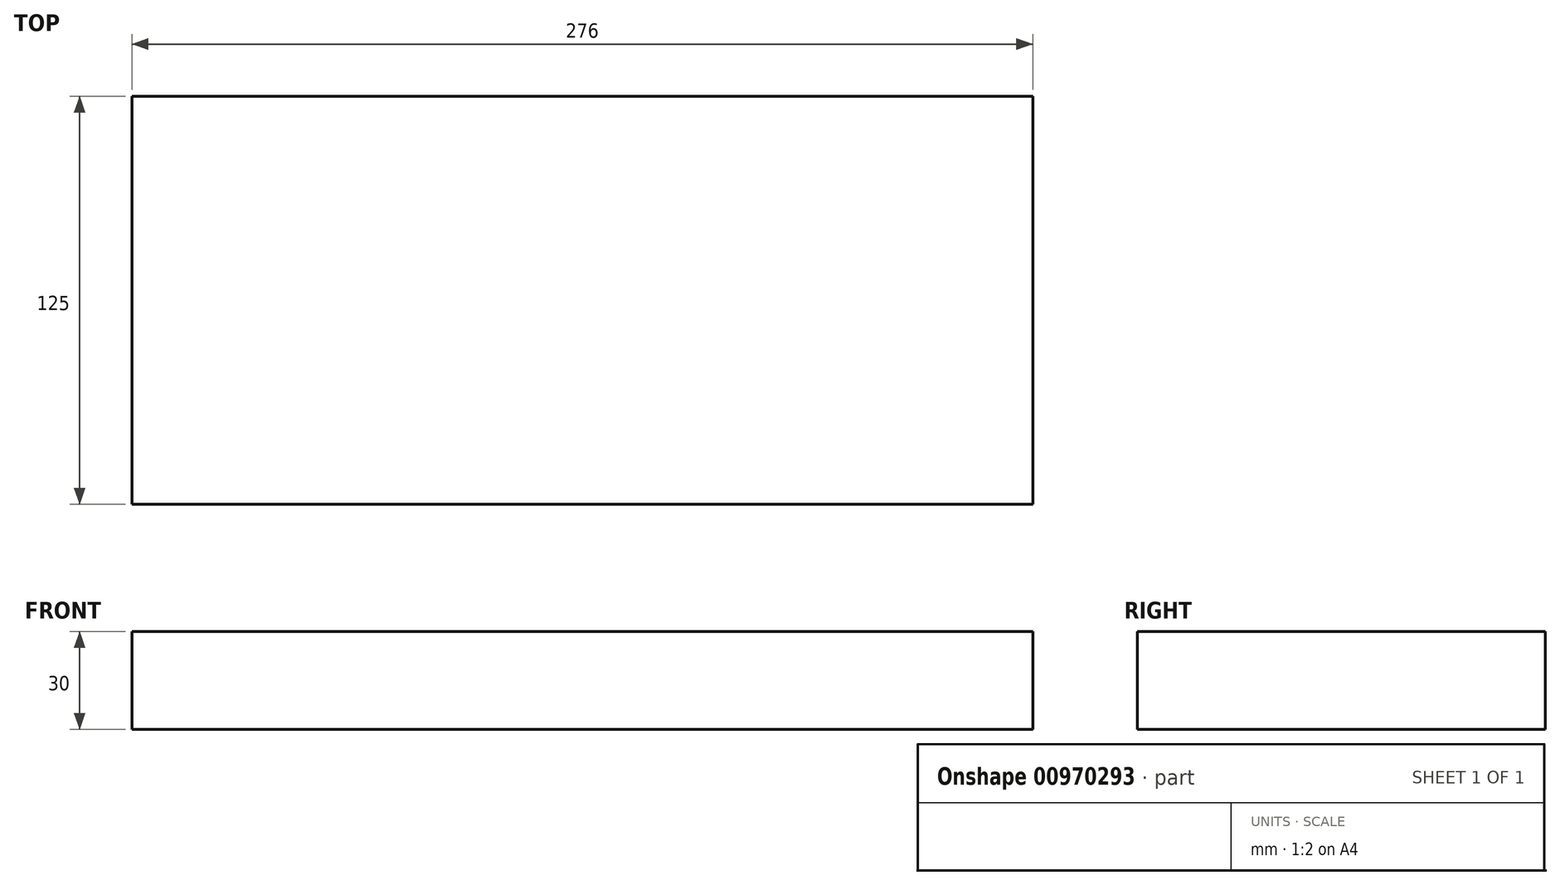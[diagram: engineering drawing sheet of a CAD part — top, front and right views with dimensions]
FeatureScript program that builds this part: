
annotation { "Feature Type Name" : "Feature", "Feature Type Description" : "" }
export const myFeature = defineFeature(function(context is Context, id is Id, definition is map)
    precondition{}
    {
        {
            var Q0;
            Q0=qCreatedBy(makeId("Top.planeOp"),FACE);
            var sketch = newSketch(context, id + "F0", { "sketchPlane" : qUnion([Q0])});
            skLineSegment(sketch, "E0.bottom", {"start": v(140.33, 62.5) * mm, "end": v(-135.67, 62.5) * mm});
            skLineSegment(sketch, "E0.top", {"start": v(140.33, -62.5) * mm, "end": v(-135.67, -62.5) * mm});
            skLineSegment(sketch, "E0.left", {"start": v(140.33, 62.5) * mm, "end": v(140.33, -62.5) * mm});
            skLineSegment(sketch, "E0.right", {"start": v(-135.67, 62.5) * mm, "end": v(-135.67, -62.5) * mm});
            skPoint(sketch, "E0.middle", {"position": v(2.33, 0) * mm});
            skSolve(sketch);
        }
        {
            var Q0;
            Q0=makeQuery(id+"F0.imprint","IMPRINT",FACE,{"disambiguationData":[TD([[makeQuery(id+"F0.imprint","IMPRINT",EDGE,{"derivedFrom":sQuery(id+"F0.wireOp",EDGE,"E0.bottom")}),1.0]])]});
            extrude(context, id + "F1", {"entities" : qUnion([Q0]), "depth" : 30 * mm, "offsetDistance" : 25.4 * mm});
        }
    });
